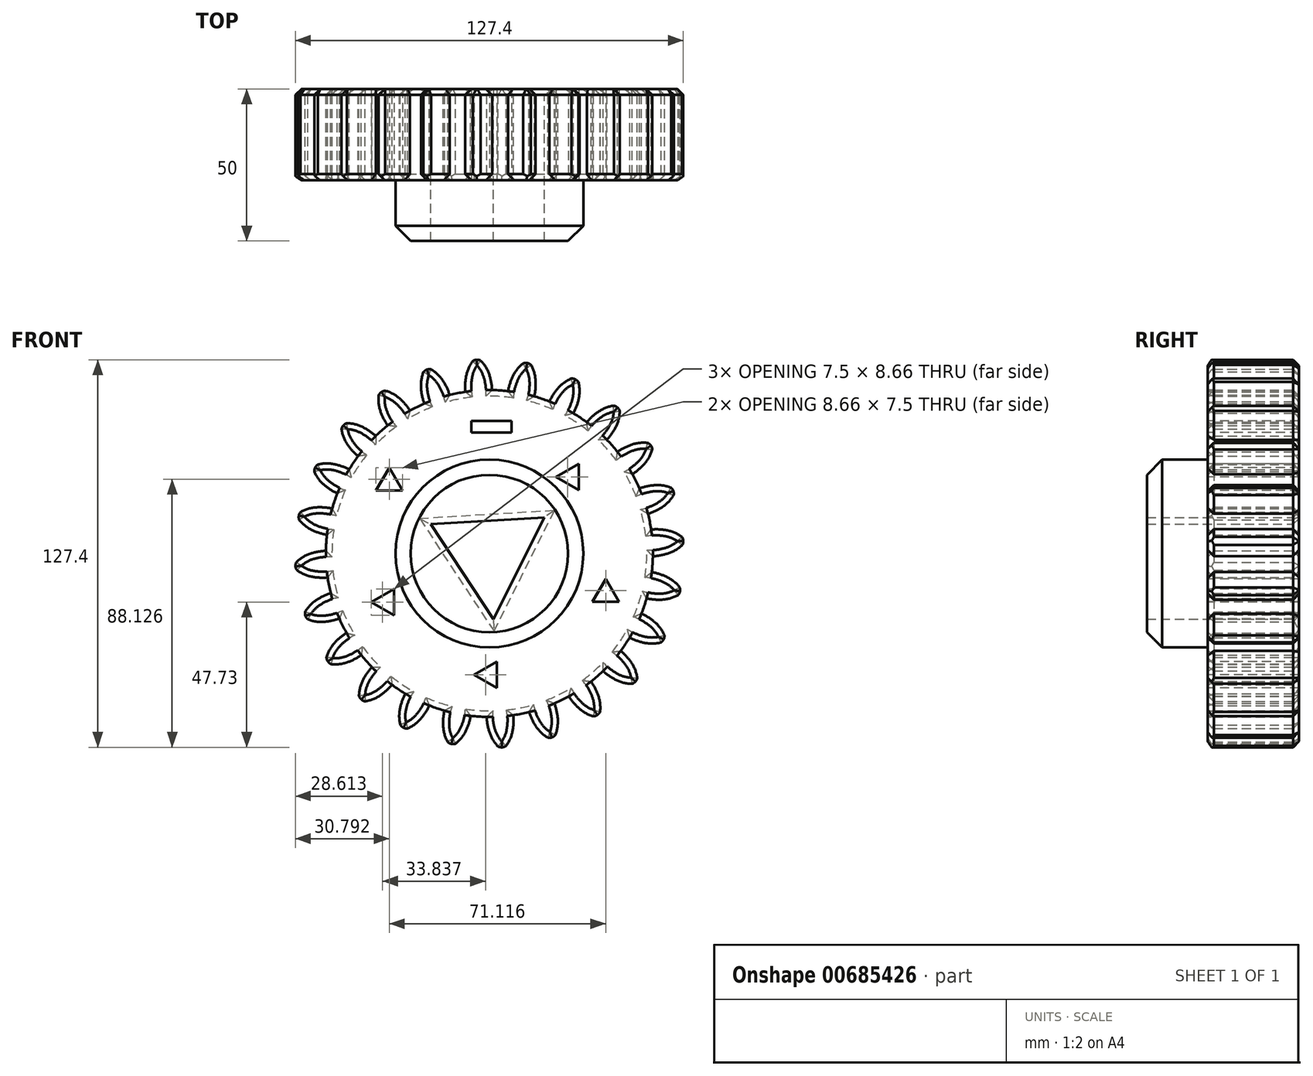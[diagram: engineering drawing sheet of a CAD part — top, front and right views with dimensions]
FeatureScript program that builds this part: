
annotation { "Feature Type Name" : "Feature", "Feature Type Description" : "" }
export const myFeature = defineFeature(function(context is Context, id is Id, definition is map)
    precondition{}
    {
        {
            var Q0;
            Q0=qCreatedBy(makeId("Front.planeOp"),FACE);
            var sketch = newSketch(context, id + "F0", { "sketchPlane" : qUnion([Q0])});
            skCircle(sketch, "E0", {"center": v(0, 0) * mm, "radius": 53.72 * mm});
            skCircle(sketch, "E1", {"center": v(0, 0) * mm, "radius": 58.67 * mm, "construction": true});
            skCircle(sketch, "E2", {"center": v(0, 0) * mm, "radius": 63.5 * mm, "construction": true});
            skLineSegment(sketch, "E3", {"start": v(0, 0) * mm, "end": v(0, 95.44) * mm, "construction": true});
            skLineSegment(sketch, "E4", {"start": v(0, 0) * mm, "end": v(-6.27, 95.6) * mm, "construction": true});
            skLineSegment(sketch, "E5", {"start": v(0, 58.67) * mm, "end": v(-75.4, 58.67) * mm, "construction": true});
            skLineSegment(sketch, "E6", {"start": v(0, 58.67) * mm, "end": v(-75.03, 31.36) * mm, "construction": true});
            skCircle(sketch, "E7", {"center": v(0, 0) * mm, "radius": 55.14 * mm, "construction": true});
            skCircle(sketch, "E8", {"center": v(0, 58.67) * mm, "radius": 14.6 * mm, "construction": true});
            skCircle(sketch, "E9", {"center": v(-13.72, 53.68) * mm, "radius": 14.6 * mm, "construction": true});
            skArc(sketch, "E10", {"start": v(0, 58.67) * mm, "mid": v(-1.15, 61.22) * mm, "end": v(-2.86, 63.44) * mm});
            skArc(sketch, "E11", {"start": v(0.88, 53.71) * mm, "mid": v(0.6, 56.22) * mm, "end": v(0, 58.67) * mm});
            skArc(sketch, "E12.MirrorCS", {"start": v(-7.66, 58.17) * mm, "mid": v(-6.85, 60.85) * mm, "end": v(-5.45, 63.27) * mm});
            skArc(sketch, "E13.MirrorCS", {"start": v(-7.88, 53.14) * mm, "mid": v(-7.94, 55.66) * mm, "end": v(-7.66, 58.17) * mm});
            skArc(sketch, "E14", {"start": v(-2.86, 63.44) * mm, "mid": v(-4.17, 63.7) * mm, "end": v(-5.45, 63.27) * mm});
            skCircle(sketch, "E15", {"center": v(0, 0) * mm, "radius": 30.86 * mm});
            skCircle(sketch, "E16.cCircle", {"center": v(0, 0) * mm, "radius": 10.79 * mm, "construction": true});
            skLineSegment(sketch, "E16.0", {"start": v(18.01, 11.88) * mm, "end": v(1.28, -21.54) * mm});
            skLineSegment(sketch, "E16.1", {"start": v(1.28, -21.54) * mm, "end": v(-19.3, 9.66) * mm});
            skLineSegment(sketch, "E16.2", {"start": v(-19.3, 9.66) * mm, "end": v(18.01, 11.88) * mm});
            skPoint(sketch, "E16.0.midPoint", {"position": v(9.65, -4.83) * mm});
            skSolve(sketch);
        }
        {
            var Q0;
            {var subQ0=sQuery(id+"F0.wireOp",EDGE,"E0");var subQ1=makeQuery(id+"F0.imprint","INTERSECT",VERTEX,{"derivedFrom":[subQ0,sQuery(id+"F0.wireOp",EDGE,"E11")]});Q0=makeQuery(id+"F0.imprint","IMPRINT",FACE,{"disambiguationData":[TD([[makeQuery(id+"F0.imprint","IMPRINT",EDGE,{"disambiguationData":[TD([[subQ1,-1.0]])],"derivedFrom":subQ0}),1.0]])]});}
            var Q1;
            Q1=makeQuery(id+"F0.imprint","IMPRINT",FACE,{"disambiguationData":[TD([[makeQuery(id+"F0.imprint","IMPRINT",EDGE,{"derivedFrom":sQuery(id+"F0.wireOp",EDGE,"E10")}),1.0]])]});
            var Q2;
            Q2=makeQuery(id+"F0.imprint","IMPRINT",FACE,{"disambiguationData":[TD([[makeQuery(id+"F0.imprint","IMPRINT",EDGE,{"derivedFrom":sQuery(id+"F0.wireOp",EDGE,"3Q0PKgbY-dWzt-37Ak-rDaJ-mU9UwyPIQOex")}),1.0]])]});
            var Q3;
            Q3=makeQuery(id+"F0.imprint","IMPRINT",FACE,{"disambiguationData":[TD([[makeQuery(id+"F0.imprint","IMPRINT",EDGE,{"derivedFrom":sQuery(id+"F0.wireOp",EDGE,"4417614c-5319-454a-a1dd-4df527e49696.0")}),-1.0]])]});
            extrude(context, id + "F1", {"entities" : qUnion([Q0, Q1, Q2, Q3]), "depth" : 30 * mm, "offsetDistance" : 25 * mm});
        }
        {
            var Q0;
            Q0=makeQuery(id+"F1.opExtrude","SWEPT_BODY",BODY,{"disambiguationData":[OSD([sQuery(id+"F0.wireOp",EDGE,"E0"),sQuery(id+"F0.wireOp",EDGE,"E10"),sQuery(id+"F0.wireOp",EDGE,"E11"),sQuery(id+"F0.wireOp",EDGE,"E12.MirrorCS"),sQuery(id+"F0.wireOp",EDGE,"E13.MirrorCS"),sQuery(id+"F0.wireOp",EDGE,"E14"),sQuery(id+"F0.wireOp",EDGE,"E15"),sQuery(id+"F0.wireOp",EDGE,"31cc62eb-3bbe-41b6-9dc2-f67773e99e41.0"),sQuery(id+"F0.wireOp",EDGE,"31cc62eb-3bbe-41b6-9dc2-f67773e99e41.1"),sQuery(id+"F0.wireOp",EDGE,"31cc62eb-3bbe-41b6-9dc2-f67773e99e41.2")])]});
            var Q1;
            Q1=makeQuery(id+"F1.opExtrude","SWEPT_FACE",FACE,{"disambiguationData":[OSD([sQuery(id+"F0.wireOp",EDGE,"E0")])]});
            circularPattern(context, id + "F2", {"entities" : qUnion([Q0]), "axis" : qUnion([Q1]), "angle" : 360 * degree, "instanceCount" : 24, "equalSpace" : true});
        }
        {
            var Q0;
            Q0=makeQuery(id+"F0.imprint","IMPRINT",FACE,{"disambiguationData":[TD([[makeQuery(id+"F0.imprint","IMPRINT",EDGE,{"derivedFrom":sQuery(id+"F0.wireOp",EDGE,"E15")}),1.0]])]});
            extrude(context, id + "F3", {"entities" : qUnion([Q0]), "operationType" : NewBodyOperationType.ADD, "depth" : 50 * mm, "offsetDistance" : 25 * mm});
        }
        {
            var Q0;
            Q0=makeQuery(id+"F1.opExtrude","CAP_EDGE",EDGE,{"disambiguationData":[OSD([sQuery(id+"F0.wireOp",EDGE,"E11")])],"isStart":false});
            var Q1;
            Q1=makeQuery(id+"F1.opExtrude","CAP_EDGE",EDGE,{"disambiguationData":[OSD([sQuery(id+"F0.wireOp",EDGE,"E13.MirrorCS")])],"isStart":false});
            var Q2;
            Q2=makeQuery(id+"F2.opPattern","COPY",EDGE,{"derivedFrom":makeQuery(id+"F1.opExtrude","CAP_EDGE",EDGE,{"disambiguationData":[OSD([sQuery(id+"F0.wireOp",EDGE,"E13.MirrorCS")])],"isStart":false}),"instanceName":"1"});
            var Q3;
            Q3=makeQuery(id+"F2.opPattern","COPY",EDGE,{"derivedFrom":makeQuery(id+"F1.opExtrude","CAP_EDGE",EDGE,{"disambiguationData":[OSD([sQuery(id+"F0.wireOp",EDGE,"E11")])],"isStart":false}),"instanceName":"1"});
            var Q4;
            Q4=makeQuery(id+"F2.opPattern","COPY",EDGE,{"derivedFrom":makeQuery(id+"F1.opExtrude","CAP_EDGE",EDGE,{"disambiguationData":[OSD([sQuery(id+"F0.wireOp",EDGE,"E13.MirrorCS")])],"isStart":false}),"instanceName":"2"});
            var Q5;
            Q5=makeQuery(id+"F2.opPattern","COPY",EDGE,{"derivedFrom":makeQuery(id+"F1.opExtrude","CAP_EDGE",EDGE,{"disambiguationData":[OSD([sQuery(id+"F0.wireOp",EDGE,"E11")])],"isStart":false}),"instanceName":"2"});
            var Q6;
            Q6=makeQuery(id+"F2.opPattern","COPY",EDGE,{"derivedFrom":makeQuery(id+"F1.opExtrude","CAP_EDGE",EDGE,{"disambiguationData":[OSD([sQuery(id+"F0.wireOp",EDGE,"E13.MirrorCS")])],"isStart":false}),"instanceName":"3"});
            var Q7;
            Q7=makeQuery(id+"F2.opPattern","COPY",EDGE,{"derivedFrom":makeQuery(id+"F1.opExtrude","CAP_EDGE",EDGE,{"disambiguationData":[OSD([sQuery(id+"F0.wireOp",EDGE,"E11")])],"isStart":false}),"instanceName":"3"});
            var Q8;
            Q8=makeQuery(id+"F2.opPattern","COPY",EDGE,{"derivedFrom":makeQuery(id+"F1.opExtrude","CAP_EDGE",EDGE,{"disambiguationData":[OSD([sQuery(id+"F0.wireOp",EDGE,"E13.MirrorCS")])],"isStart":false}),"instanceName":"4"});
            var Q9;
            Q9=makeQuery(id+"F2.opPattern","COPY",EDGE,{"derivedFrom":makeQuery(id+"F1.opExtrude","CAP_EDGE",EDGE,{"disambiguationData":[OSD([sQuery(id+"F0.wireOp",EDGE,"E11")])],"isStart":false}),"instanceName":"4"});
            var Q10;
            Q10=makeQuery(id+"F2.opPattern","COPY",EDGE,{"derivedFrom":makeQuery(id+"F1.opExtrude","CAP_EDGE",EDGE,{"disambiguationData":[OSD([sQuery(id+"F0.wireOp",EDGE,"E13.MirrorCS")])],"isStart":false}),"instanceName":"5"});
            var Q11;
            Q11=makeQuery(id+"F2.opPattern","COPY",EDGE,{"derivedFrom":makeQuery(id+"F1.opExtrude","CAP_EDGE",EDGE,{"disambiguationData":[OSD([sQuery(id+"F0.wireOp",EDGE,"E11")])],"isStart":false}),"instanceName":"5"});
            var Q12;
            Q12=makeQuery(id+"F2.opPattern","COPY",EDGE,{"derivedFrom":makeQuery(id+"F1.opExtrude","CAP_EDGE",EDGE,{"disambiguationData":[OSD([sQuery(id+"F0.wireOp",EDGE,"E13.MirrorCS")])],"isStart":false}),"instanceName":"6"});
            var Q13;
            Q13=makeQuery(id+"F2.opPattern","COPY",EDGE,{"derivedFrom":makeQuery(id+"F1.opExtrude","CAP_EDGE",EDGE,{"disambiguationData":[OSD([sQuery(id+"F0.wireOp",EDGE,"E11")])],"isStart":false}),"instanceName":"6"});
            var Q14;
            Q14=makeQuery(id+"F2.opPattern","COPY",EDGE,{"derivedFrom":makeQuery(id+"F1.opExtrude","CAP_EDGE",EDGE,{"disambiguationData":[OSD([sQuery(id+"F0.wireOp",EDGE,"E13.MirrorCS")])],"isStart":false}),"instanceName":"7"});
            var Q15;
            Q15=makeQuery(id+"F2.opPattern","COPY",EDGE,{"derivedFrom":makeQuery(id+"F1.opExtrude","CAP_EDGE",EDGE,{"disambiguationData":[OSD([sQuery(id+"F0.wireOp",EDGE,"E11")])],"isStart":false}),"instanceName":"7"});
            var Q16;
            Q16=makeQuery(id+"F2.opPattern","COPY",EDGE,{"derivedFrom":makeQuery(id+"F1.opExtrude","CAP_EDGE",EDGE,{"disambiguationData":[OSD([sQuery(id+"F0.wireOp",EDGE,"E13.MirrorCS")])],"isStart":false}),"instanceName":"8"});
            var Q17;
            Q17=makeQuery(id+"F2.opPattern","COPY",EDGE,{"derivedFrom":makeQuery(id+"F1.opExtrude","CAP_EDGE",EDGE,{"disambiguationData":[OSD([sQuery(id+"F0.wireOp",EDGE,"E11")])],"isStart":false}),"instanceName":"8"});
            var Q18;
            Q18=makeQuery(id+"F2.opPattern","COPY",EDGE,{"derivedFrom":makeQuery(id+"F1.opExtrude","SWEPT_EDGE",EDGE,{"disambiguationData":[OSD([sQuery(id+"F0.wireOp",EDGE,"E12.MirrorCS"),sQuery(id+"F0.wireOp",EDGE,"E13.MirrorCS")])]}),"instanceName":"9"});
            var Q19;
            Q19=makeQuery(id+"F2.opPattern","COPY",EDGE,{"derivedFrom":makeQuery(id+"F1.opExtrude","CAP_EDGE",EDGE,{"disambiguationData":[OSD([sQuery(id+"F0.wireOp",EDGE,"E13.MirrorCS")])],"isStart":false}),"instanceName":"9"});
            var Q20;
            Q20=makeQuery(id+"F2.opPattern","COPY",EDGE,{"derivedFrom":makeQuery(id+"F1.opExtrude","CAP_EDGE",EDGE,{"disambiguationData":[OSD([sQuery(id+"F0.wireOp",EDGE,"E11")])],"isStart":false}),"instanceName":"9"});
            var Q21;
            Q21=makeQuery(id+"F2.opPattern","COPY",EDGE,{"derivedFrom":makeQuery(id+"F1.opExtrude","CAP_EDGE",EDGE,{"disambiguationData":[OSD([sQuery(id+"F0.wireOp",EDGE,"E13.MirrorCS")])],"isStart":false}),"instanceName":"10"});
            var Q22;
            Q22=makeQuery(id+"F2.opPattern","COPY",EDGE,{"derivedFrom":makeQuery(id+"F1.opExtrude","CAP_EDGE",EDGE,{"disambiguationData":[OSD([sQuery(id+"F0.wireOp",EDGE,"E11")])],"isStart":false}),"instanceName":"10"});
            var Q23;
            Q23=makeQuery(id+"F2.opPattern","COPY",EDGE,{"derivedFrom":makeQuery(id+"F1.opExtrude","CAP_EDGE",EDGE,{"disambiguationData":[OSD([sQuery(id+"F0.wireOp",EDGE,"E13.MirrorCS")])],"isStart":false}),"instanceName":"11"});
            var Q24;
            Q24=makeQuery(id+"F2.opPattern","COPY",EDGE,{"derivedFrom":makeQuery(id+"F1.opExtrude","CAP_EDGE",EDGE,{"disambiguationData":[OSD([sQuery(id+"F0.wireOp",EDGE,"E11")])],"isStart":false}),"instanceName":"11"});
            var Q25;
            Q25=makeQuery(id+"F2.opPattern","COPY",EDGE,{"derivedFrom":makeQuery(id+"F1.opExtrude","CAP_EDGE",EDGE,{"disambiguationData":[OSD([sQuery(id+"F0.wireOp",EDGE,"E13.MirrorCS")])],"isStart":false}),"instanceName":"12"});
            var Q26;
            Q26=makeQuery(id+"F2.opPattern","COPY",EDGE,{"derivedFrom":makeQuery(id+"F1.opExtrude","CAP_EDGE",EDGE,{"disambiguationData":[OSD([sQuery(id+"F0.wireOp",EDGE,"E11")])],"isStart":false}),"instanceName":"12"});
            var Q27;
            Q27=makeQuery(id+"F2.opPattern","COPY",EDGE,{"derivedFrom":makeQuery(id+"F1.opExtrude","CAP_EDGE",EDGE,{"disambiguationData":[OSD([sQuery(id+"F0.wireOp",EDGE,"E13.MirrorCS")])],"isStart":false}),"instanceName":"13"});
            var Q28;
            Q28=makeQuery(id+"F2.opPattern","COPY",EDGE,{"derivedFrom":makeQuery(id+"F1.opExtrude","CAP_EDGE",EDGE,{"disambiguationData":[OSD([sQuery(id+"F0.wireOp",EDGE,"E11")])],"isStart":false}),"instanceName":"13"});
            var Q29;
            Q29=makeQuery(id+"F2.opPattern","COPY",EDGE,{"derivedFrom":makeQuery(id+"F1.opExtrude","CAP_EDGE",EDGE,{"disambiguationData":[OSD([sQuery(id+"F0.wireOp",EDGE,"E13.MirrorCS")])],"isStart":false}),"instanceName":"14"});
            var Q30;
            Q30=makeQuery(id+"F2.opPattern","COPY",EDGE,{"derivedFrom":makeQuery(id+"F1.opExtrude","CAP_EDGE",EDGE,{"disambiguationData":[OSD([sQuery(id+"F0.wireOp",EDGE,"E11")])],"isStart":false}),"instanceName":"14"});
            var Q31;
            Q31=makeQuery(id+"F2.opPattern","COPY",EDGE,{"derivedFrom":makeQuery(id+"F1.opExtrude","CAP_EDGE",EDGE,{"disambiguationData":[OSD([sQuery(id+"F0.wireOp",EDGE,"E13.MirrorCS")])],"isStart":false}),"instanceName":"15"});
            var Q32;
            Q32=makeQuery(id+"F2.opPattern","COPY",EDGE,{"derivedFrom":makeQuery(id+"F1.opExtrude","CAP_EDGE",EDGE,{"disambiguationData":[OSD([sQuery(id+"F0.wireOp",EDGE,"E11")])],"isStart":false}),"instanceName":"15"});
            var Q33;
            Q33=makeQuery(id+"F2.opPattern","COPY",EDGE,{"derivedFrom":makeQuery(id+"F1.opExtrude","CAP_EDGE",EDGE,{"disambiguationData":[OSD([sQuery(id+"F0.wireOp",EDGE,"E13.MirrorCS")])],"isStart":false}),"instanceName":"16"});
            var Q34;
            Q34=makeQuery(id+"F2.opPattern","COPY",EDGE,{"derivedFrom":makeQuery(id+"F1.opExtrude","CAP_EDGE",EDGE,{"disambiguationData":[OSD([sQuery(id+"F0.wireOp",EDGE,"E11")])],"isStart":false}),"instanceName":"16"});
            var Q35;
            Q35=makeQuery(id+"F2.opPattern","COPY",EDGE,{"derivedFrom":makeQuery(id+"F1.opExtrude","CAP_EDGE",EDGE,{"disambiguationData":[OSD([sQuery(id+"F0.wireOp",EDGE,"E13.MirrorCS")])],"isStart":false}),"instanceName":"17"});
            var Q36;
            Q36=makeQuery(id+"F2.opPattern","COPY",EDGE,{"derivedFrom":makeQuery(id+"F1.opExtrude","CAP_EDGE",EDGE,{"disambiguationData":[OSD([sQuery(id+"F0.wireOp",EDGE,"E11")])],"isStart":false}),"instanceName":"17"});
            var Q37;
            Q37=makeQuery(id+"F2.opPattern","COPY",EDGE,{"derivedFrom":makeQuery(id+"F1.opExtrude","CAP_EDGE",EDGE,{"disambiguationData":[OSD([sQuery(id+"F0.wireOp",EDGE,"E13.MirrorCS")])],"isStart":false}),"instanceName":"18"});
            var Q38;
            Q38=makeQuery(id+"F2.opPattern","COPY",EDGE,{"derivedFrom":makeQuery(id+"F1.opExtrude","CAP_EDGE",EDGE,{"disambiguationData":[OSD([sQuery(id+"F0.wireOp",EDGE,"E11")])],"isStart":false}),"instanceName":"18"});
            var Q39;
            Q39=makeQuery(id+"F2.opPattern","COPY",EDGE,{"derivedFrom":makeQuery(id+"F1.opExtrude","CAP_EDGE",EDGE,{"disambiguationData":[OSD([sQuery(id+"F0.wireOp",EDGE,"E13.MirrorCS")])],"isStart":false}),"instanceName":"19"});
            var Q40;
            Q40=makeQuery(id+"F2.opPattern","COPY",EDGE,{"derivedFrom":makeQuery(id+"F1.opExtrude","CAP_EDGE",EDGE,{"disambiguationData":[OSD([sQuery(id+"F0.wireOp",EDGE,"E11")])],"isStart":false}),"instanceName":"19"});
            var Q41;
            Q41=makeQuery(id+"F2.opPattern","COPY",EDGE,{"derivedFrom":makeQuery(id+"F1.opExtrude","CAP_EDGE",EDGE,{"disambiguationData":[OSD([sQuery(id+"F0.wireOp",EDGE,"E13.MirrorCS")])],"isStart":false}),"instanceName":"20"});
            var Q42;
            Q42=makeQuery(id+"F2.opPattern","COPY",EDGE,{"derivedFrom":makeQuery(id+"F1.opExtrude","CAP_EDGE",EDGE,{"disambiguationData":[OSD([sQuery(id+"F0.wireOp",EDGE,"E11")])],"isStart":false}),"instanceName":"20"});
            var Q43;
            Q43=makeQuery(id+"F2.opPattern","COPY",EDGE,{"derivedFrom":makeQuery(id+"F1.opExtrude","CAP_EDGE",EDGE,{"disambiguationData":[OSD([sQuery(id+"F0.wireOp",EDGE,"E13.MirrorCS")])],"isStart":false}),"instanceName":"21"});
            var Q44;
            Q44=makeQuery(id+"F2.opPattern","COPY",EDGE,{"derivedFrom":makeQuery(id+"F1.opExtrude","CAP_EDGE",EDGE,{"disambiguationData":[OSD([sQuery(id+"F0.wireOp",EDGE,"E11")])],"isStart":false}),"instanceName":"21"});
            var Q45;
            Q45=makeQuery(id+"F2.opPattern","COPY",EDGE,{"derivedFrom":makeQuery(id+"F1.opExtrude","CAP_EDGE",EDGE,{"disambiguationData":[OSD([sQuery(id+"F0.wireOp",EDGE,"E13.MirrorCS")])],"isStart":false}),"instanceName":"22"});
            var Q46;
            Q46=makeQuery(id+"F2.opPattern","COPY",EDGE,{"derivedFrom":makeQuery(id+"F1.opExtrude","CAP_EDGE",EDGE,{"disambiguationData":[OSD([sQuery(id+"F0.wireOp",EDGE,"E11")])],"isStart":false}),"instanceName":"22"});
            var Q47;
            Q47=makeQuery(id+"F2.opPattern","COPY",EDGE,{"derivedFrom":makeQuery(id+"F1.opExtrude","CAP_EDGE",EDGE,{"disambiguationData":[OSD([sQuery(id+"F0.wireOp",EDGE,"E13.MirrorCS")])],"isStart":false}),"instanceName":"23"});
            var Q48;
            Q48=makeQuery(id+"F2.opPattern","COPY",EDGE,{"derivedFrom":makeQuery(id+"F1.opExtrude","CAP_EDGE",EDGE,{"disambiguationData":[OSD([sQuery(id+"F0.wireOp",EDGE,"E11")])],"isStart":false}),"instanceName":"23"});
            var Q49;
            {var subQ0=sQuery(id+"F0.wireOp",EDGE,"E15");var subQ1=makeQuery(id+"F1.opExtrude","CAP_FACE",FACE,{"disambiguationData":[OSD([sQuery(id+"F0.wireOp",EDGE,"E0"),sQuery(id+"F0.wireOp",EDGE,"E10"),sQuery(id+"F0.wireOp",EDGE,"E11"),sQuery(id+"F0.wireOp",EDGE,"E12.MirrorCS"),sQuery(id+"F0.wireOp",EDGE,"E13.MirrorCS"),sQuery(id+"F0.wireOp",EDGE,"E14"),subQ0])],"isStart":true});Q49=makeQuery(id+"F3.boolean.opBoolean","MERGE",FACE,{"derivedFrom":[subQ1,makeQuery(id+"F2.opPattern","COPY",FACE,{"derivedFrom":subQ1,"instanceName":"1"}),makeQuery(id+"F2.opPattern","COPY",FACE,{"derivedFrom":subQ1,"instanceName":"2"}),makeQuery(id+"F2.opPattern","COPY",FACE,{"derivedFrom":subQ1,"instanceName":"3"}),makeQuery(id+"F2.opPattern","COPY",FACE,{"derivedFrom":subQ1,"instanceName":"4"}),makeQuery(id+"F2.opPattern","COPY",FACE,{"derivedFrom":subQ1,"instanceName":"5"}),makeQuery(id+"F2.opPattern","COPY",FACE,{"derivedFrom":subQ1,"instanceName":"6"}),makeQuery(id+"F2.opPattern","COPY",FACE,{"derivedFrom":subQ1,"instanceName":"7"}),makeQuery(id+"F2.opPattern","COPY",FACE,{"derivedFrom":subQ1,"instanceName":"8"}),makeQuery(id+"F2.opPattern","COPY",FACE,{"derivedFrom":subQ1,"instanceName":"9"}),makeQuery(id+"F2.opPattern","COPY",FACE,{"derivedFrom":subQ1,"instanceName":"10"}),makeQuery(id+"F2.opPattern","COPY",FACE,{"derivedFrom":subQ1,"instanceName":"11"}),makeQuery(id+"F2.opPattern","COPY",FACE,{"derivedFrom":subQ1,"instanceName":"12"}),makeQuery(id+"F2.opPattern","COPY",FACE,{"derivedFrom":subQ1,"instanceName":"13"}),makeQuery(id+"F2.opPattern","COPY",FACE,{"derivedFrom":subQ1,"instanceName":"14"}),makeQuery(id+"F2.opPattern","COPY",FACE,{"derivedFrom":subQ1,"instanceName":"15"}),makeQuery(id+"F2.opPattern","COPY",FACE,{"derivedFrom":subQ1,"instanceName":"16"}),makeQuery(id+"F2.opPattern","COPY",FACE,{"derivedFrom":subQ1,"instanceName":"17"}),makeQuery(id+"F2.opPattern","COPY",FACE,{"derivedFrom":subQ1,"instanceName":"18"}),makeQuery(id+"F2.opPattern","COPY",FACE,{"derivedFrom":subQ1,"instanceName":"19"}),makeQuery(id+"F2.opPattern","COPY",FACE,{"derivedFrom":subQ1,"instanceName":"20"}),makeQuery(id+"F2.opPattern","COPY",FACE,{"derivedFrom":subQ1,"instanceName":"21"}),makeQuery(id+"F2.opPattern","COPY",FACE,{"derivedFrom":subQ1,"instanceName":"22"}),makeQuery(id+"F2.opPattern","COPY",FACE,{"derivedFrom":subQ1,"instanceName":"23"}),makeQuery(id+"F3.opExtrude","CAP_FACE",FACE,{"disambiguationData":[OSD([sQuery(id+"F0.wireOp",EDGE,"19ae24a6-e92d-4116-b942-5415395ed2d1.0"),sQuery(id+"F0.wireOp",EDGE,"19ae24a6-e92d-4116-b942-5415395ed2d1.1"),sQuery(id+"F0.wireOp",EDGE,"19ae24a6-e92d-4116-b942-5415395ed2d1.2"),sQuery(id+"F0.wireOp",EDGE,"19ae24a6-e92d-4116-b942-5415395ed2d1.3"),sQuery(id+"F0.wireOp",EDGE,"19ae24a6-e92d-4116-b942-5415395ed2d1.4"),subQ0])],"isStart":true})]});}
            chamfer(context, id + "F4", {"entities" : qUnion([Q0, Q1, Q2, Q3, Q4, Q5, Q6, Q7, Q8, Q9, Q10, Q11, Q12, Q13, Q14, Q15, Q16, Q17, Q18, Q19, Q20, Q21, Q22, Q23, Q24, Q25, Q26, Q27, Q28, Q29, Q30, Q31, Q32, Q33, Q34, Q35, Q36, Q37, Q38, Q39, Q40, Q41, Q42, Q43, Q44, Q45, Q46, Q47, Q48, Q49]), "width" : 2 * mm, "tangentPropagation" : true});
        }
        {
            var Q0;
            {var subQ0=makeQuery(id+"F1.opExtrude","CAP_FACE",FACE,{"disambiguationData":[OSD([sQuery(id+"F0.wireOp",EDGE,"E0"),sQuery(id+"F0.wireOp",EDGE,"E10"),sQuery(id+"F0.wireOp",EDGE,"E11"),sQuery(id+"F0.wireOp",EDGE,"E12.MirrorCS"),sQuery(id+"F0.wireOp",EDGE,"E13.MirrorCS"),sQuery(id+"F0.wireOp",EDGE,"E14"),sQuery(id+"F0.wireOp",EDGE,"E15")])],"isStart":false});Q0=makeQuery(id+"F3.boolean.opBoolean","MERGE",FACE,{"derivedFrom":[subQ0,makeQuery(id+"F2.opPattern","COPY",FACE,{"derivedFrom":subQ0,"instanceName":"1"}),makeQuery(id+"F2.opPattern","COPY",FACE,{"derivedFrom":subQ0,"instanceName":"2"}),makeQuery(id+"F2.opPattern","COPY",FACE,{"derivedFrom":subQ0,"instanceName":"3"}),makeQuery(id+"F2.opPattern","COPY",FACE,{"derivedFrom":subQ0,"instanceName":"4"}),makeQuery(id+"F2.opPattern","COPY",FACE,{"derivedFrom":subQ0,"instanceName":"5"}),makeQuery(id+"F2.opPattern","COPY",FACE,{"derivedFrom":subQ0,"instanceName":"6"}),makeQuery(id+"F2.opPattern","COPY",FACE,{"derivedFrom":subQ0,"instanceName":"7"}),makeQuery(id+"F2.opPattern","COPY",FACE,{"derivedFrom":subQ0,"instanceName":"8"}),makeQuery(id+"F2.opPattern","COPY",FACE,{"derivedFrom":subQ0,"instanceName":"9"}),makeQuery(id+"F2.opPattern","COPY",FACE,{"derivedFrom":subQ0,"instanceName":"10"}),makeQuery(id+"F2.opPattern","COPY",FACE,{"derivedFrom":subQ0,"instanceName":"11"}),makeQuery(id+"F2.opPattern","COPY",FACE,{"derivedFrom":subQ0,"instanceName":"12"}),makeQuery(id+"F2.opPattern","COPY",FACE,{"derivedFrom":subQ0,"instanceName":"13"}),makeQuery(id+"F2.opPattern","COPY",FACE,{"derivedFrom":subQ0,"instanceName":"14"}),makeQuery(id+"F2.opPattern","COPY",FACE,{"derivedFrom":subQ0,"instanceName":"15"}),makeQuery(id+"F2.opPattern","COPY",FACE,{"derivedFrom":subQ0,"instanceName":"16"}),makeQuery(id+"F2.opPattern","COPY",FACE,{"derivedFrom":subQ0,"instanceName":"17"}),makeQuery(id+"F2.opPattern","COPY",FACE,{"derivedFrom":subQ0,"instanceName":"18"}),makeQuery(id+"F2.opPattern","COPY",FACE,{"derivedFrom":subQ0,"instanceName":"19"}),makeQuery(id+"F2.opPattern","COPY",FACE,{"derivedFrom":subQ0,"instanceName":"20"}),makeQuery(id+"F2.opPattern","COPY",FACE,{"derivedFrom":subQ0,"instanceName":"21"}),makeQuery(id+"F2.opPattern","COPY",FACE,{"derivedFrom":subQ0,"instanceName":"22"}),makeQuery(id+"F2.opPattern","COPY",FACE,{"derivedFrom":subQ0,"instanceName":"23"})]});}
            var sketch = newSketch(context, id + "F5", { "sketchPlane" : qUnion([Q0])});
            skLineSegment(sketch, "E17.bottom", {"start": v(0, 43.6) * mm, "end": v(7.22, 43.6) * mm});
            skLineSegment(sketch, "E17.top", {"start": v(0, 39.75) * mm, "end": v(7.22, 39.75) * mm});
            skLineSegment(sketch, "E17.left", {"start": v(0, 43.6) * mm, "end": v(0, 39.75) * mm});
            skLineSegment(sketch, "E17.right", {"start": v(7.22, 43.6) * mm, "end": v(7.22, 39.75) * mm});
            skLineSegment(sketch, "E18.bottom", {"start": v(0, 43.6) * mm, "end": v(-5.9, 43.6) * mm});
            skLineSegment(sketch, "E18.top", {"start": v(0, 39.82) * mm, "end": v(-5.9, 39.82) * mm});
            skLineSegment(sketch, "E18.left", {"start": v(0, 43.6) * mm, "end": v(0, 39.82) * mm});
            skLineSegment(sketch, "E18.right", {"start": v(-5.9, 43.6) * mm, "end": v(-5.9, 39.82) * mm});
            skCircle(sketch, "E19.cCircle", {"center": v(26.9, 25.17) * mm, "radius": 2.5 * mm, "construction": true});
            skLineSegment(sketch, "E19.0", {"start": v(29.4, 29.5) * mm, "end": v(29.4, 20.84) * mm});
            skLineSegment(sketch, "E19.1", {"start": v(29.4, 20.84) * mm, "end": v(21.9, 25.17) * mm});
            skLineSegment(sketch, "E19.2", {"start": v(21.9, 25.17) * mm, "end": v(29.4, 29.5) * mm});
            skPoint(sketch, "E19.0.midPoint", {"position": v(29.4, 25.17) * mm});
            skCircle(sketch, "E20.cCircle", {"center": v(38.2, -13.4) * mm, "radius": 2.5 * mm, "construction": true});
            skLineSegment(sketch, "E20.0", {"start": v(42.54, -15.9) * mm, "end": v(33.88, -15.9) * mm});
            skLineSegment(sketch, "E20.1", {"start": v(33.88, -15.9) * mm, "end": v(38.2, -8.4) * mm});
            skLineSegment(sketch, "E20.2", {"start": v(38.2, -8.4) * mm, "end": v(42.54, -15.9) * mm});
            skPoint(sketch, "E20.0.midPoint", {"position": v(38.2, -15.9) * mm});
            skCircle(sketch, "E21.cCircle", {"center": v(0, -39.88) * mm, "radius": 2.5 * mm, "construction": true});
            skLineSegment(sketch, "E21.0", {"start": v(2.5, -35.55) * mm, "end": v(2.5, -44.2) * mm});
            skLineSegment(sketch, "E21.1", {"start": v(2.5, -44.2) * mm, "end": v(-5, -39.88) * mm});
            skLineSegment(sketch, "E21.2", {"start": v(-5, -39.88) * mm, "end": v(2.5, -35.55) * mm});
            skPoint(sketch, "E21.0.midPoint", {"position": v(2.5, -39.88) * mm});
            skCircle(sketch, "E22.cCircle", {"center": v(-33.84, -15.97) * mm, "radius": 2.5 * mm, "construction": true});
            skLineSegment(sketch, "E22.0", {"start": v(-31.34, -11.64) * mm, "end": v(-31.34, -20.3) * mm});
            skLineSegment(sketch, "E22.1", {"start": v(-31.34, -20.3) * mm, "end": v(-38.84, -15.97) * mm});
            skLineSegment(sketch, "E22.2", {"start": v(-38.84, -15.97) * mm, "end": v(-31.34, -11.64) * mm});
            skPoint(sketch, "E22.0.midPoint", {"position": v(-31.34, -15.97) * mm});
            skCircle(sketch, "E23.cCircle", {"center": v(-32.9, 23.18) * mm, "radius": 2.5 * mm, "construction": true});
            skLineSegment(sketch, "E23.0", {"start": v(-28.58, 20.68) * mm, "end": v(-37.24, 20.68) * mm});
            skLineSegment(sketch, "E23.1", {"start": v(-37.24, 20.68) * mm, "end": v(-32.9, 28.18) * mm});
            skLineSegment(sketch, "E23.2", {"start": v(-32.9, 28.18) * mm, "end": v(-28.58, 20.68) * mm});
            skPoint(sketch, "E23.0.midPoint", {"position": v(-32.9, 20.68) * mm});
            skSolve(sketch);
        }
        {
            var Q0;
            Q0=makeQuery(id+"F5.imprint","IMPRINT",FACE,{"disambiguationData":[TD([[makeQuery(id+"F5.imprint","IMPRINT",EDGE,{"derivedFrom":sQuery(id+"F5.wireOp",EDGE,"E17.bottom")}),-1.0]])]});
            var Q1;
            Q1=makeQuery(id+"F5.imprint","IMPRINT",FACE,{"disambiguationData":[TD([[makeQuery(id+"F5.imprint","IMPRINT",EDGE,{"derivedFrom":sQuery(id+"F5.wireOp",EDGE,"E18.bottom")}),1.0]])]});
            var Q2;
            Q2=makeQuery(id+"F5.imprint","IMPRINT",FACE,{"disambiguationData":[TD([[makeQuery(id+"F5.imprint","IMPRINT",EDGE,{"derivedFrom":sQuery(id+"F5.wireOp",EDGE,"E19.0")}),-1.0]])]});
            var Q3;
            Q3=makeQuery(id+"F5.imprint","IMPRINT",FACE,{"disambiguationData":[TD([[makeQuery(id+"F5.imprint","IMPRINT",EDGE,{"derivedFrom":sQuery(id+"F5.wireOp",EDGE,"E20.0")}),-1.0]])]});
            var Q4;
            Q4=makeQuery(id+"F5.imprint","IMPRINT",FACE,{"disambiguationData":[TD([[makeQuery(id+"F5.imprint","IMPRINT",EDGE,{"derivedFrom":sQuery(id+"F5.wireOp",EDGE,"E21.0")}),-1.0]])]});
            var Q5;
            Q5=makeQuery(id+"F5.imprint","IMPRINT",FACE,{"disambiguationData":[TD([[makeQuery(id+"F5.imprint","IMPRINT",EDGE,{"derivedFrom":sQuery(id+"F5.wireOp",EDGE,"E22.0")}),-1.0]])]});
            var Q6;
            Q6=makeQuery(id+"F5.imprint","IMPRINT",FACE,{"disambiguationData":[TD([[makeQuery(id+"F5.imprint","IMPRINT",EDGE,{"derivedFrom":sQuery(id+"F5.wireOp",EDGE,"E23.0")}),-1.0]])]});
            extrude(context, id + "F6", {"entities" : qUnion([Q0, Q1, Q2, Q3, Q4, Q5, Q6]), "operationType" : NewBodyOperationType.REMOVE, "oppositeDirection" : true, "depth" : 63 * mm, "offsetDistance" : 25 * mm});
        }
        {
            var Q0;
            Q0=makeQuery(id+"F3.opExtrude","CAP_EDGE",EDGE,{"disambiguationData":[OSD([sQuery(id+"F0.wireOp",EDGE,"E15")])],"isStart":false});
            chamfer(context, id + "F7", {"entities" : qUnion([Q0]), "width" : 5 * mm, "tangentPropagation" : true});
        }
    });
